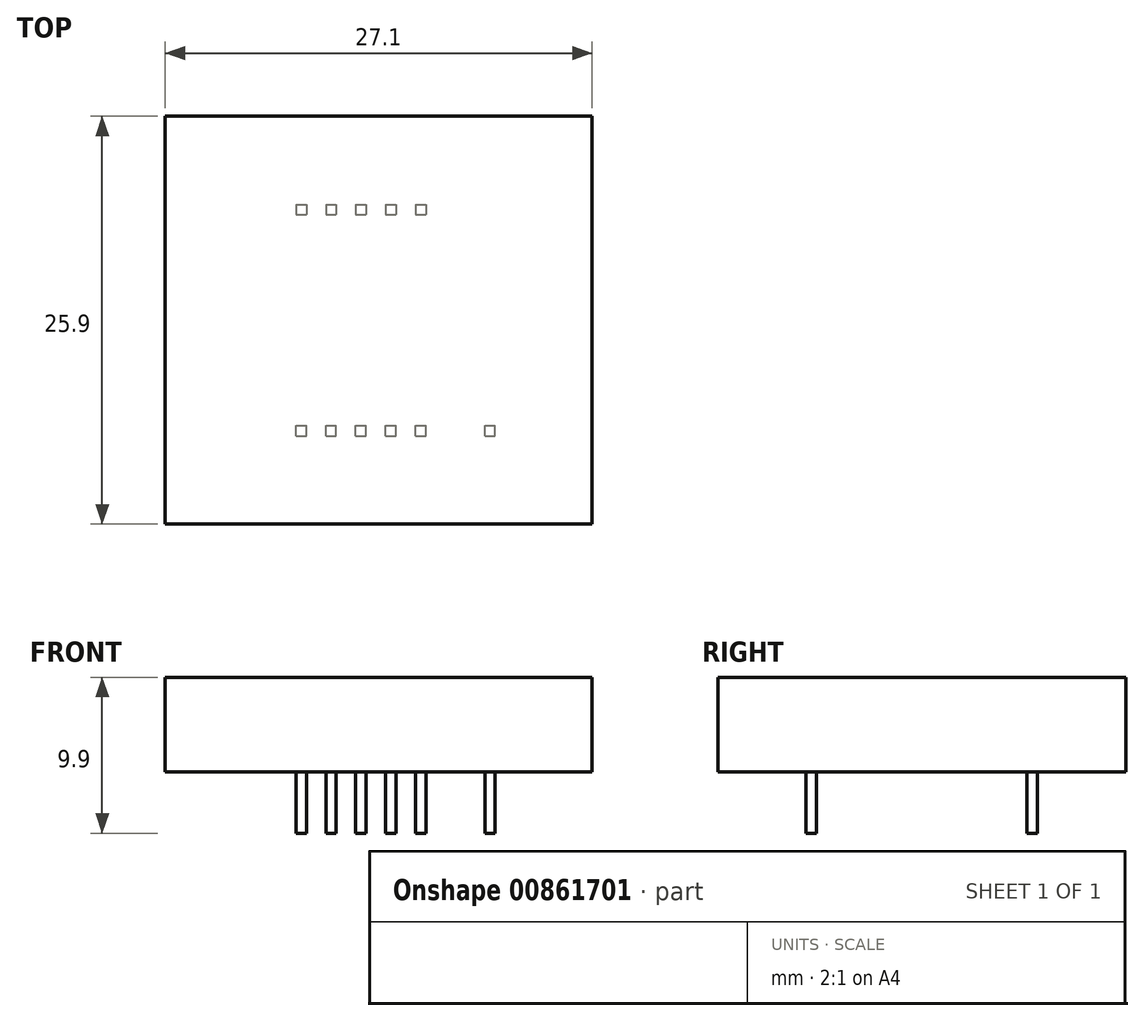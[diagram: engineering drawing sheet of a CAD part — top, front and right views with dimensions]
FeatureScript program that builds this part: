
annotation { "Feature Type Name" : "Feature", "Feature Type Description" : "" }
export const myFeature = defineFeature(function(context is Context, id is Id, definition is map)
    precondition{}
    {
        {
            var Q0;
            Q0=qCreatedBy(makeId("Top.planeOp"),FACE);
            var sketch = newSketch(context, id + "F0", { "sketchPlane" : qUnion([Q0])});
            skLineSegment(sketch, "E0.bottom", {"start": v(13.55, 12.95) * mm, "end": v(-13.55, 12.95) * mm});
            skLineSegment(sketch, "E0.top", {"start": v(13.55, -12.95) * mm, "end": v(-13.55, -12.95) * mm});
            skLineSegment(sketch, "E0.left", {"start": v(13.55, 12.95) * mm, "end": v(13.55, -12.95) * mm});
            skLineSegment(sketch, "E0.right", {"start": v(-13.55, 12.95) * mm, "end": v(-13.55, -12.95) * mm});
            skPoint(sketch, "E0.middle", {"position": v(0, 0) * mm});
            skSolve(sketch);
        }
        {
            var Q0;
            Q0=makeQuery(id+"F0.imprint","IMPRINT",FACE,{"disambiguationData":[TD([[makeQuery(id+"F0.imprint","IMPRINT",EDGE,{"derivedFrom":sQuery(id+"F0.wireOp",EDGE,"E0.bottom")}),1.0]])]});
            extrude(context, id + "F1", {"entities" : qUnion([Q0]), "depth" : 6 * mm, "offsetDistance" : 25 * mm});
        }
        {
            var Q0;
            Q0=makeQuery(id+"F1.opExtrude","CAP_FACE",FACE,{"disambiguationData":[OSD([sQuery(id+"F0.wireOp",EDGE,"E0.bottom"),sQuery(id+"F0.wireOp",EDGE,"E0.top"),sQuery(id+"F0.wireOp",EDGE,"E0.left"),sQuery(id+"F0.wireOp",EDGE,"E0.right")])],"isStart":true});
            var sketch = newSketch(context, id + "F2", { "sketchPlane" : qUnion([Q0])});
            skLineSegment(sketch, "E1.bottom", {"start": v(-5.25, 7.35) * mm, "end": v(-4.6, 7.35) * mm});
            skLineSegment(sketch, "E1.top", {"start": v(-5.25, 6.69) * mm, "end": v(-4.6, 6.69) * mm});
            skLineSegment(sketch, "E1.left", {"start": v(-5.25, 7.35) * mm, "end": v(-5.25, 6.69) * mm});
            skLineSegment(sketch, "E1.right", {"start": v(-4.6, 7.35) * mm, "end": v(-4.6, 6.69) * mm});
            skLineSegment(sketch, "E2.1.0.0", {"start": v(-2.7, 7.35) * mm, "end": v(-2.7, 6.69) * mm});
            skLineSegment(sketch, "E2.1.0.1", {"start": v(-3.35, 6.69) * mm, "end": v(-2.7, 6.69) * mm});
            skLineSegment(sketch, "E2.1.0.2", {"start": v(-3.35, 7.35) * mm, "end": v(-3.35, 6.69) * mm});
            skLineSegment(sketch, "E2.1.0.3", {"start": v(-3.35, 7.35) * mm, "end": v(-2.7, 7.35) * mm});
            skLineSegment(sketch, "E2.2.0.0", {"start": v(-0.8, 7.35) * mm, "end": v(-0.8, 6.69) * mm});
            skLineSegment(sketch, "E2.2.0.1", {"start": v(-1.45, 6.69) * mm, "end": v(-0.8, 6.69) * mm});
            skLineSegment(sketch, "E2.2.0.2", {"start": v(-1.45, 7.35) * mm, "end": v(-1.45, 6.69) * mm});
            skLineSegment(sketch, "E2.2.0.3", {"start": v(-1.45, 7.35) * mm, "end": v(-0.8, 7.35) * mm});
            skLineSegment(sketch, "E2.3.0.0", {"start": v(1.1, 7.35) * mm, "end": v(1.1, 6.69) * mm});
            skLineSegment(sketch, "E2.3.0.1", {"start": v(0.45, 6.69) * mm, "end": v(1.1, 6.69) * mm});
            skLineSegment(sketch, "E2.3.0.2", {"start": v(0.45, 7.35) * mm, "end": v(0.45, 6.69) * mm});
            skLineSegment(sketch, "E2.3.0.3", {"start": v(0.45, 7.35) * mm, "end": v(1.1, 7.35) * mm});
            skLineSegment(sketch, "E2.4.0.0", {"start": v(3, 7.35) * mm, "end": v(3, 6.69) * mm});
            skLineSegment(sketch, "E2.4.0.1", {"start": v(2.35, 6.69) * mm, "end": v(3, 6.69) * mm});
            skLineSegment(sketch, "E2.4.0.2", {"start": v(2.35, 7.35) * mm, "end": v(2.35, 6.69) * mm});
            skLineSegment(sketch, "E2.4.0.3", {"start": v(2.35, 7.35) * mm, "end": v(3, 7.35) * mm});
            skLineSegment(sketch, "E2.direction1", {"start": v(-4.6, 6.69) * mm, "end": v(-2.7, 6.69) * mm, "construction": true});
            skLineSegment(sketch, "E3.MirrorCS", {"start": v(-3.35, -6.69) * mm, "end": v(-2.7, -6.69) * mm});
            skLineSegment(sketch, "E4.MirrorCS", {"start": v(-2.7, -7.35) * mm, "end": v(-2.7, -6.69) * mm});
            skLineSegment(sketch, "E5.MirrorCS", {"start": v(-3.35, -7.35) * mm, "end": v(-2.7, -7.35) * mm});
            skLineSegment(sketch, "E6.MirrorCS", {"start": v(-3.35, -7.35) * mm, "end": v(-3.35, -6.69) * mm});
            skLineSegment(sketch, "E7.MirrorCS", {"start": v(-4.6, -7.35) * mm, "end": v(-4.6, -6.69) * mm});
            skLineSegment(sketch, "E8.MirrorCS", {"start": v(-4.6, -6.69) * mm, "end": v(-2.7, -6.69) * mm, "construction": true});
            skLineSegment(sketch, "E9.MirrorCS", {"start": v(-5.25, -6.69) * mm, "end": v(-4.6, -6.69) * mm});
            skLineSegment(sketch, "E10.MirrorCS", {"start": v(-5.25, -7.35) * mm, "end": v(-4.6, -7.35) * mm});
            skLineSegment(sketch, "E11.MirrorCS", {"start": v(3, -7.35) * mm, "end": v(3, -6.69) * mm});
            skLineSegment(sketch, "E12.MirrorCS", {"start": v(2.35, -6.69) * mm, "end": v(3, -6.69) * mm});
            skLineSegment(sketch, "E13.MirrorCS", {"start": v(1.1, -7.35) * mm, "end": v(1.1, -6.69) * mm});
            skLineSegment(sketch, "E14.MirrorCS", {"start": v(0.45, -7.35) * mm, "end": v(0.45, -6.69) * mm});
            skLineSegment(sketch, "E15.MirrorCS", {"start": v(2.35, -7.35) * mm, "end": v(2.35, -6.69) * mm});
            skLineSegment(sketch, "E16.MirrorCS", {"start": v(-1.45, -7.35) * mm, "end": v(-0.8, -7.35) * mm});
            skLineSegment(sketch, "E17.MirrorCS", {"start": v(0.45, -6.69) * mm, "end": v(1.1, -6.69) * mm});
            skLineSegment(sketch, "E18.MirrorCS", {"start": v(2.35, -7.35) * mm, "end": v(3, -7.35) * mm});
            skLineSegment(sketch, "E19.MirrorCS", {"start": v(-1.45, -7.35) * mm, "end": v(-1.45, -6.69) * mm});
            skLineSegment(sketch, "E20.MirrorCS", {"start": v(0.45, -7.35) * mm, "end": v(1.1, -7.35) * mm});
            skLineSegment(sketch, "E21.MirrorCS", {"start": v(-1.45, -6.69) * mm, "end": v(-0.8, -6.69) * mm});
            skLineSegment(sketch, "E22.MirrorCS", {"start": v(-5.25, -7.35) * mm, "end": v(-5.25, -6.69) * mm});
            skLineSegment(sketch, "E23.MirrorCS", {"start": v(-0.8, -7.35) * mm, "end": v(-0.8, -6.69) * mm});
            skLineSegment(sketch, "E24.4.0.0", {"start": v(7.4, 7.35) * mm, "end": v(7.4, 6.69) * mm});
            skLineSegment(sketch, "E24.4.0.1", {"start": v(6.75, 6.69) * mm, "end": v(7.4, 6.69) * mm});
            skLineSegment(sketch, "E24.4.0.2", {"start": v(6.75, 7.35) * mm, "end": v(6.75, 6.7) * mm});
            skLineSegment(sketch, "E24.4.0.3", {"start": v(6.75, 7.35) * mm, "end": v(7.4, 7.35) * mm});
            skSolve(sketch);
        }
        {
            var Q0;
            Q0=makeQuery(id+"F2.imprint","IMPRINT",FACE,{"disambiguationData":[TD([[makeQuery(id+"F2.imprint","IMPRINT",EDGE,{"derivedFrom":sQuery(id+"F2.wireOp",EDGE,"E2.1.0.0")}),-1.0]])]});
            var Q1;
            Q1=makeQuery(id+"F2.imprint","IMPRINT",FACE,{"disambiguationData":[TD([[makeQuery(id+"F2.imprint","IMPRINT",EDGE,{"derivedFrom":sQuery(id+"F2.wireOp",EDGE,"E2.2.0.0")}),-1.0]])]});
            var Q2;
            Q2=makeQuery(id+"F2.imprint","IMPRINT",FACE,{"disambiguationData":[TD([[makeQuery(id+"F2.imprint","IMPRINT",EDGE,{"derivedFrom":sQuery(id+"F2.wireOp",EDGE,"E2.3.0.0")}),-1.0]])]});
            var Q3;
            Q3=makeQuery(id+"F2.imprint","IMPRINT",FACE,{"disambiguationData":[TD([[makeQuery(id+"F2.imprint","IMPRINT",EDGE,{"derivedFrom":sQuery(id+"F2.wireOp",EDGE,"E2.4.0.0")}),-1.0]])]});
            var Q4;
            Q4=makeQuery(id+"F2.imprint","IMPRINT",FACE,{"disambiguationData":[TD([[makeQuery(id+"F2.imprint","IMPRINT",EDGE,{"derivedFrom":sQuery(id+"F2.wireOp",EDGE,"E3.MirrorCS")}),-1.0]])]});
            var Q5;
            Q5=makeQuery(id+"F2.imprint","IMPRINT",FACE,{"disambiguationData":[TD([[makeQuery(id+"F2.imprint","IMPRINT",EDGE,{"derivedFrom":sQuery(id+"F2.wireOp",EDGE,"E7.MirrorCS")}),1.0]])]});
            var Q6;
            Q6=makeQuery(id+"F2.imprint","IMPRINT",FACE,{"disambiguationData":[TD([[makeQuery(id+"F2.imprint","IMPRINT",EDGE,{"derivedFrom":sQuery(id+"F2.wireOp",EDGE,"E11.MirrorCS")}),1.0]])]});
            var Q7;
            Q7=makeQuery(id+"F2.imprint","IMPRINT",FACE,{"disambiguationData":[TD([[makeQuery(id+"F2.imprint","IMPRINT",EDGE,{"derivedFrom":sQuery(id+"F2.wireOp",EDGE,"E13.MirrorCS")}),1.0]])]});
            var Q8;
            Q8=makeQuery(id+"F2.imprint","IMPRINT",FACE,{"disambiguationData":[TD([[makeQuery(id+"F2.imprint","IMPRINT",EDGE,{"derivedFrom":sQuery(id+"F2.wireOp",EDGE,"E16.MirrorCS")}),1.0]])]});
            var Q9;
            Q9=makeQuery(id+"F2.imprint","IMPRINT",FACE,{"disambiguationData":[TD([[makeQuery(id+"F2.imprint","IMPRINT",EDGE,{"derivedFrom":sQuery(id+"F2.wireOp",EDGE,"E24.4.0.0")}),-1.0]])]});
            var Q10;
            Q10=makeQuery(id+"F2.imprint","IMPRINT",FACE,{"disambiguationData":[TD([[makeQuery(id+"F2.imprint","IMPRINT",EDGE,{"derivedFrom":sQuery(id+"F2.wireOp",EDGE,"E1.bottom")}),-1.0]])]});
            extrude(context, id + "F3", {"entities" : qUnion([Q0, Q1, Q2, Q3, Q4, Q5, Q6, Q7, Q8, Q9, Q10]), "depth" : (9.9 - 6) * mm, "offsetDistance" : 25 * mm});
        }
    });
